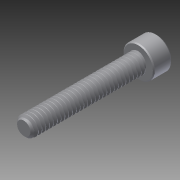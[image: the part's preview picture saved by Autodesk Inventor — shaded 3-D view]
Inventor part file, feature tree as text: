
AUTODESK INVENTOR PART (.ipt)
format: ipt  version: 2015 (Build 190159000, 159)  size: 864,256 bytes
history: native  units: in
note: dims shown in document units (in); Inventor stores cm internally (conversion verified against a paired STEP export)
features: chamfer x1, other x1, imported_body x1
ambient origin geometry x8: Origin, YZ Plane, XZ Plane, XY Plane, X Axis, Y Axis, Z Axis, Center Point
bodies: Body1 (feature_tree)
feature tree (3):
  chamfer  "Chamfer2"  [1 undecoded]
  other  "91251A1311"
  imported_body  "Base1"
note: 1 required parameter value undecoded (feature->parameter linkage not recoverable at this tier; creation-order binding heuristic only, values carry confidence <= 0.55)
